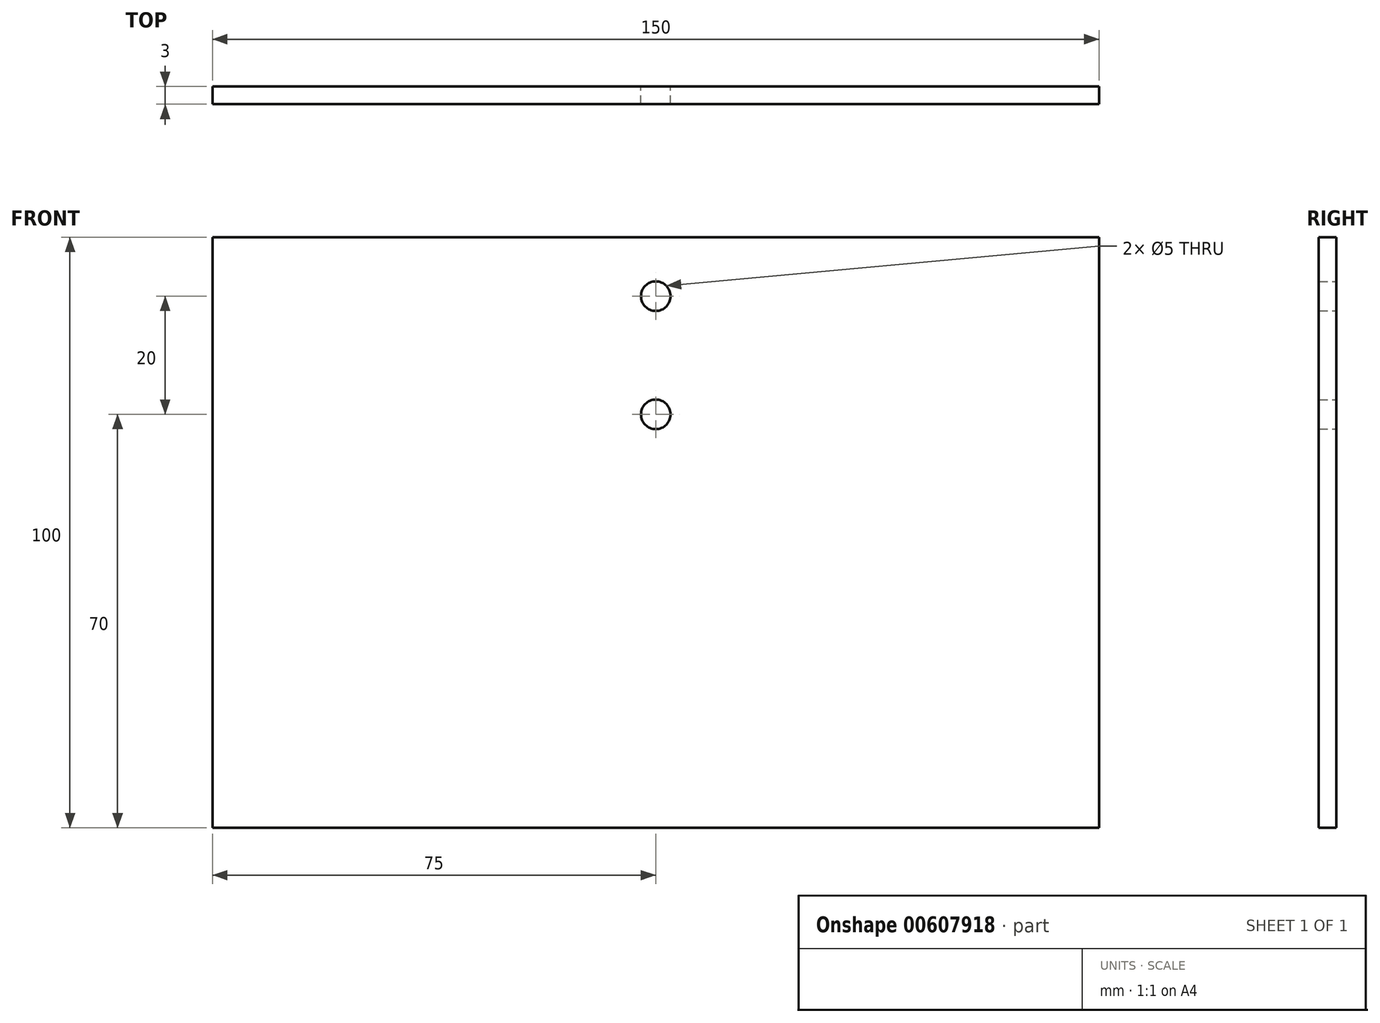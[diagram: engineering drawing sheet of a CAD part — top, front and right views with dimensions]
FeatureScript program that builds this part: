
annotation { "Feature Type Name" : "Feature", "Feature Type Description" : "" }
export const myFeature = defineFeature(function(context is Context, id is Id, definition is map)
    precondition{}
    {
        {
            var Q0;
            Q0=qCreatedBy(makeId("Front.planeOp"),FACE);
            var sketch = newSketch(context, id + "F0", { "sketchPlane" : qUnion([Q0])});
            skLineSegment(sketch, "E0.bottom", {"start": v(0, 0) * mm, "end": v(150, 0) * mm});
            skLineSegment(sketch, "E0.top", {"start": v(0, -100) * mm, "end": v(150, -100) * mm});
            skLineSegment(sketch, "E0.left", {"start": v(0, 0) * mm, "end": v(0, -100) * mm});
            skLineSegment(sketch, "E0.right", {"start": v(150, 0) * mm, "end": v(150, -100) * mm});
            skLineSegment(sketch, "E1", {"start": v(75, 0) * mm, "end": v(75, -100) * mm, "construction": true});
            skLineSegment(sketch, "E2", {"start": v(0, -50) * mm, "end": v(150, -50) * mm, "construction": true});
            skCircle(sketch, "E3", {"center": v(75, -10) * mm, "radius": 2.5 * mm});
            skCircle(sketch, "E4", {"center": v(75, -30) * mm, "radius": 2.5 * mm});
            skSolve(sketch);
        }
        {
            var Q0;
            Q0 = qSketchRegion(id + "F0", true);
            extrude(context, id + "F1", {"entities" : qUnion([Q0]), "depth" : 3 * mm, "offsetDistance" : 25 * mm});
        }
    });
